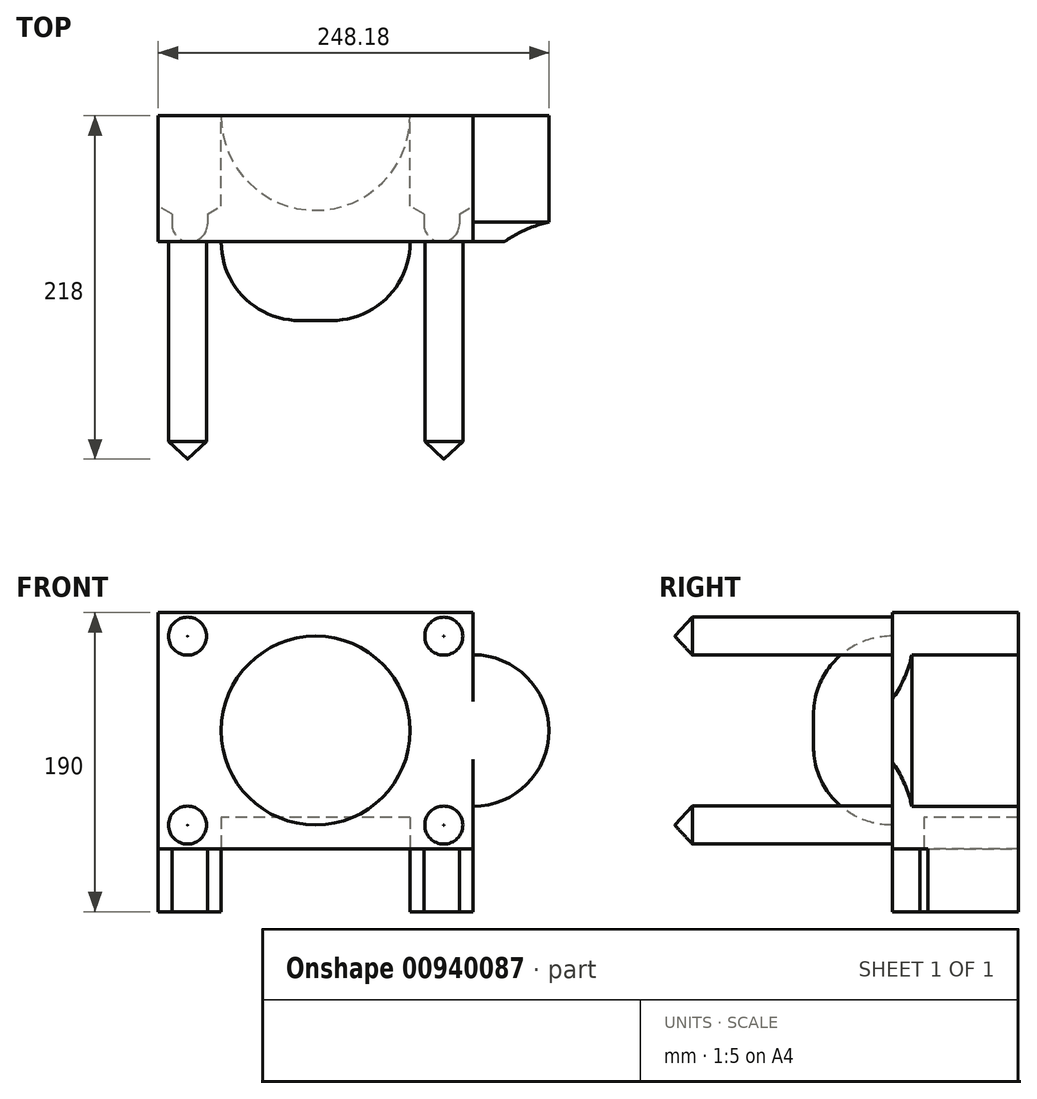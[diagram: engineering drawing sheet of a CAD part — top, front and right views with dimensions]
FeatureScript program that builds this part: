
annotation { "Feature Type Name" : "Feature", "Feature Type Description" : "" }
export const myFeature = defineFeature(function(context is Context, id is Id, definition is map)
    precondition{}
    {
        {
            var Q0;
            Q0=qCreatedBy(makeId("Front.planeOp"),FACE);
            var sketch = newSketch(context, id + "F0", { "sketchPlane" : qUnion([Q0])});
            skLineSegment(sketch, "E0.bottom", {"start": v(100, -75) * mm, "end": v(-100, -75) * mm});
            skLineSegment(sketch, "E0.top", {"start": v(100, 75) * mm, "end": v(-100, 75) * mm});
            skLineSegment(sketch, "E0.left", {"start": v(100, -75) * mm, "end": v(100, 75) * mm});
            skLineSegment(sketch, "E0.right", {"start": v(-100, -75) * mm, "end": v(-100, 75) * mm});
            skPoint(sketch, "E0.middle", {"position": v(0, 0) * mm});
            skCircle(sketch, "E1", {"center": v(-81.38, 60) * mm, "radius": 12.07 * mm});
            skCircle(sketch, "E2", {"center": v(81.38, 60) * mm, "radius": 12.07 * mm});
            skCircle(sketch, "E3", {"center": v(81.38, -60) * mm, "radius": 12.07 * mm});
            skCircle(sketch, "E4", {"center": v(-81.38, -60) * mm, "radius": 12.07 * mm});
            skCircle(sketch, "E5", {"center": v(0, 0) * mm, "radius": 60 * mm});
            skSolve(sketch);
        }
        {
            var Q0;
            Q0=makeQuery(id+"F0.imprint","IMPRINT",FACE,{"disambiguationData":[TD([[makeQuery(id+"F0.imprint","IMPRINT",EDGE,{"derivedFrom":sQuery(id+"F0.wireOp",EDGE,"E3")}),1.0]])]});
            var Q1;
            Q1=makeQuery(id+"F0.imprint","IMPRINT",FACE,{"disambiguationData":[TD([[makeQuery(id+"F0.imprint","IMPRINT",EDGE,{"derivedFrom":sQuery(id+"F0.wireOp",EDGE,"E1")}),1.0]])]});
            var Q2;
            Q2=makeQuery(id+"F0.imprint","IMPRINT",FACE,{"disambiguationData":[TD([[makeQuery(id+"F0.imprint","IMPRINT",EDGE,{"derivedFrom":sQuery(id+"F0.wireOp",EDGE,"E5")}),1.0]])]});
            var Q3;
            Q3=makeQuery(id+"F0.imprint","IMPRINT",FACE,{"disambiguationData":[TD([[makeQuery(id+"F0.imprint","IMPRINT",EDGE,{"derivedFrom":sQuery(id+"F0.wireOp",EDGE,"E4")}),1.0]])]});
            var Q4;
            Q4=makeQuery(id+"F0.imprint","IMPRINT",FACE,{"disambiguationData":[TD([[makeQuery(id+"F0.imprint","IMPRINT",EDGE,{"derivedFrom":sQuery(id+"F0.wireOp",EDGE,"E2")}),1.0]])]});
            var Q5;
            Q5=makeQuery(id+"F0.imprint","IMPRINT",FACE,{"disambiguationData":[TD([[makeQuery(id+"F0.imprint","IMPRINT",EDGE,{"derivedFrom":sQuery(id+"F0.wireOp",EDGE,"E0.bottom")}),-1.0]])]});
            extrude(context, id + "F1", {"entities" : qUnion([Q0, Q1, Q2, Q3, Q4, Q5]), "oppositeDirection" : true, "depth" : 80 * mm, "offsetDistance" : 25 * mm});
        }
        {
            var Q0;
            Q0=makeQuery(id+"F0.imprint","IMPRINT",FACE,{"disambiguationData":[TD([[makeQuery(id+"F0.imprint","IMPRINT",EDGE,{"derivedFrom":sQuery(id+"F0.wireOp",EDGE,"E1")}),1.0]])]});
            var Q1;
            Q1=makeQuery(id+"F0.imprint","IMPRINT",FACE,{"disambiguationData":[TD([[makeQuery(id+"F0.imprint","IMPRINT",EDGE,{"derivedFrom":sQuery(id+"F0.wireOp",EDGE,"E2")}),1.0]])]});
            var Q2;
            Q2=makeQuery(id+"F0.imprint","IMPRINT",FACE,{"disambiguationData":[TD([[makeQuery(id+"F0.imprint","IMPRINT",EDGE,{"derivedFrom":sQuery(id+"F0.wireOp",EDGE,"E3")}),1.0]])]});
            var Q3;
            Q3=makeQuery(id+"F0.imprint","IMPRINT",FACE,{"disambiguationData":[TD([[makeQuery(id+"F0.imprint","IMPRINT",EDGE,{"derivedFrom":sQuery(id+"F0.wireOp",EDGE,"E4")}),1.0]])]});
            extrude(context, id + "F2", {"entities" : qUnion([Q0, Q1, Q2, Q3]), "operationType" : NewBodyOperationType.ADD, "depth" : 138 * mm, "offsetDistance" : 25 * mm});
        }
        {
            var Q0;
            Q0=makeQuery(id+"F2.opExtrude","CAP_FACE",FACE,{"disambiguationData":[OSD([sQuery(id+"F0.wireOp",EDGE,"E1")])],"isStart":false});
            var Q1;
            Q1=makeQuery(id+"F2.opExtrude","CAP_FACE",FACE,{"disambiguationData":[OSD([sQuery(id+"F0.wireOp",EDGE,"E4")])],"isStart":false});
            var Q2;
            Q2=makeQuery(id+"F2.opExtrude","CAP_FACE",FACE,{"disambiguationData":[OSD([sQuery(id+"F0.wireOp",EDGE,"E3")])],"isStart":false});
            var Q3;
            Q3=makeQuery(id+"F2.opExtrude","CAP_FACE",FACE,{"disambiguationData":[OSD([sQuery(id+"F0.wireOp",EDGE,"E2")])],"isStart":false});
            chamfer(context, id + "F3", {"entities" : qUnion([Q0, Q1, Q2, Q3]), "chamferType" : ChamferType.TWO_OFFSETS, "width1" : 12 * mm, "oppositeDirection" : false, "width2" : 11 * mm, "tangentPropagation" : true});
        }
        {
            var Q0;
            Q0=makeQuery(id+"F0.imprint","IMPRINT",FACE,{"disambiguationData":[TD([[makeQuery(id+"F0.imprint","IMPRINT",EDGE,{"derivedFrom":sQuery(id+"F0.wireOp",EDGE,"E5")}),1.0]])]});
            extrude(context, id + "F4", {"entities" : qUnion([Q0]), "operationType" : NewBodyOperationType.ADD, "depth" : 50 * mm, "offsetDistance" : 25 * mm});
        }
        {
            var Q0;
            Q0=makeQuery(id+"F4.opExtrude","CAP_FACE",FACE,{"disambiguationData":[OSD([sQuery(id+"F0.wireOp",EDGE,"E5")])],"isStart":false});
            fillet(context, id + "F5", {"entities" : qUnion([Q0]), "tangentPropagation" : true, "radius" : 49.73 * mm, "defaultsChanged" : true, "vertexSettings" : [], "allowEdgeOverflow" : false});
        }
        {
            var Q0;
            Q0=makeQuery(id+"F1.opExtrude","SWEPT_FACE",FACE,{"disambiguationData":[OSD([sQuery(id+"F0.wireOp",EDGE,"E0.bottom")])]});
            var sketch = newSketch(context, id + "F6", { "sketchPlane" : qUnion([Q0])});
            skLineSegment(sketch, "E6.bottom", {"start": v(-60, 0) * mm, "end": v(-100, 0) * mm});
            skLineSegment(sketch, "E6.top", {"start": v(-60, -80) * mm, "end": v(-100, -80) * mm});
            skLineSegment(sketch, "E6.left", {"start": v(-60, 0) * mm, "end": v(-60, -80) * mm});
            skLineSegment(sketch, "E6.right", {"start": v(-100, 0) * mm, "end": v(-100, -80) * mm});
            skLineSegment(sketch, "E7.MirrorCS", {"start": v(60, 0) * mm, "end": v(60, -80) * mm});
            skLineSegment(sketch, "E8.MirrorCS", {"start": v(60, 0) * mm, "end": v(100, 0) * mm});
            skLineSegment(sketch, "E9.MirrorCS", {"start": v(100, 0) * mm, "end": v(100, -80) * mm});
            skLineSegment(sketch, "E10.MirrorCS", {"start": v(60, -80) * mm, "end": v(100, -80) * mm});
            skLineSegment(sketch, "E11", {"start": v(-91.32, -17.73) * mm, "end": v(-91.32, -11.32) * mm});
            skLineSegment(sketch, "E12", {"start": v(-68.68, -17.73) * mm, "end": v(-68.68, -11.32) * mm});
            skLineSegment(sketch, "E13", {"start": v(-91.32, -17.73) * mm, "end": v(-100, -22.65) * mm});
            skLineSegment(sketch, "E14", {"start": v(-68.68, -17.73) * mm, "end": v(-60, -22.65) * mm});
            skArc(sketch, "E15", {"start": v(-68.68, -11.32) * mm, "mid": v(-80, 0) * mm, "end": v(-91.32, -11.32) * mm});
            skLineSegment(sketch, "E16.MirrorCS", {"start": v(91.32, -17.73) * mm, "end": v(100, -22.65) * mm});
            skLineSegment(sketch, "E17.MirrorCS", {"start": v(91.32, -17.73) * mm, "end": v(91.32, -11.32) * mm});
            skArc(sketch, "E18.MirrorCS", {"start": v(68.68, -11.32) * mm, "mid": v(80, 0) * mm, "end": v(91.32, -11.32) * mm});
            skLineSegment(sketch, "E19.MirrorCS", {"start": v(68.68, -17.73) * mm, "end": v(68.68, -11.32) * mm});
            skLineSegment(sketch, "E20.MirrorCS", {"start": v(68.68, -17.73) * mm, "end": v(60, -22.65) * mm});
            skArc(sketch, "E21", {"start": v(60, -80) * mm, "mid": v(0, -20) * mm, "end": v(-60, -80) * mm});
            skSolve(sketch);
        }
        {
            var Q0;
            {var subQ2=sQuery(id+"F6.wireOp",EDGE,"E6.top");Q0=makeQuery(id+"F6.imprint","IMPRINT",FACE,{"disambiguationData":[TD([[makeQuery(id+"F6.imprint","IMPRINT",EDGE,{"derivedFrom":subQ2}),-1.0]])]});}
            var Q1;
            {var subQ1=sQuery(id+"F6.wireOp",EDGE,"E10.MirrorCS");Q1=makeQuery(id+"F6.imprint","IMPRINT",FACE,{"disambiguationData":[TD([[makeQuery(id+"F6.imprint","IMPRINT",EDGE,{"derivedFrom":subQ1}),-1.0]])]});}
            extrude(context, id + "F7", {"entities" : qUnion([Q0, Q1]), "operationType" : NewBodyOperationType.ADD, "depth" : 40 * mm, "offsetDistance" : 25 * mm});
        }
        {
            var Q0;
            {var subQ0=sQuery(id+"F6.wireOp",EDGE,"E21");Q0=makeQuery(id+"F6.imprint","IMPRINT",FACE,{"disambiguationData":[TD([[makeQuery(id+"F6.imprint","IMPRINT",EDGE,{"derivedFrom":subQ0}),1.0]])]});}
            extrude(context, id + "F8", {"entities" : qUnion([Q0]), "operationType" : NewBodyOperationType.REMOVE, "oppositeDirection" : true, "depth" : 20 * mm, "offsetDistance" : 25 * mm});
        }
        {
            var Q0;
            Q0=makeQuery(id+"F7.boolean.opBoolean","MERGE",FACE,{"derivedFrom":[makeQuery(id+"F1.opExtrude","SWEPT_FACE",FACE,{"disambiguationData":[OSD([sQuery(id+"F0.wireOp",EDGE,"E0.left")])]}),makeQuery(id+"F7.opExtrude","SWEPT_FACE",FACE,{"disambiguationData":[OSD([sQuery(id+"F6.wireOp",EDGE,"E9.MirrorCS")])]})]});
            var sketch = newSketch(context, id + "F9", { "sketchPlane" : qUnion([Q0])});
            skLineSegment(sketch, "E22", {"start": v(0, 0) * mm, "end": v(80, 0) * mm});
            skLineSegment(sketch, "E23", {"start": v(0, 0) * mm, "end": v(0, -20) * mm});
            skArc(sketch, "E24", {"start": v(12.43, -48.18) * mm, "mid": v(7.73, -33.42) * mm, "end": v(0, -20) * mm});
            skLineSegment(sketch, "E25", {"start": v(80, -48.18) * mm, "end": v(12.43, -48.18) * mm});
            skSolve(sketch);
        }
        {
            var Q0;
            {var subQ1=sQuery(id+"F9.wireOp",EDGE,"E22");Q0=makeQuery(id+"F9.imprint","IMPRINT",FACE,{"disambiguationData":[TD([[makeQuery(id+"F9.imprint","IMPRINT",EDGE,{"derivedFrom":subQ1}),-1.0]])]});}
            var Q1;
            Q1=sQuery(id+"F9.wireOp",EDGE,"E22");
            revolve(context, id + "F10", {"operationType" : NewBodyOperationType.ADD, "surfaceOperationType" : NewSurfaceOperationType.NEW, "entities" : qUnion([Q0]), "axis" : qUnion([Q1]), "revolveType" : RevolveType.FULL});
        }
        {
            var Q0;
            Q0=makeQuery(id+"F10.opRevolve","SWEPT_EDGE",EDGE,{"disambiguationData":[OSD([sQuery(id+"F0.wireOp",EDGE,"E0.left"),sQuery(id+"F9.wireOp",EDGE,"E23"),sQuery(id+"F9.wireOp",EDGE,"E24")])]});
            fillet(context, id + "F11", {"entities" : qUnion([Q0]), "tangentPropagation" : true, "radius" : 5 * mm, "defaultsChanged" : false, "vertexSettings" : [], "allowEdgeOverflow" : false});
        }
    });
